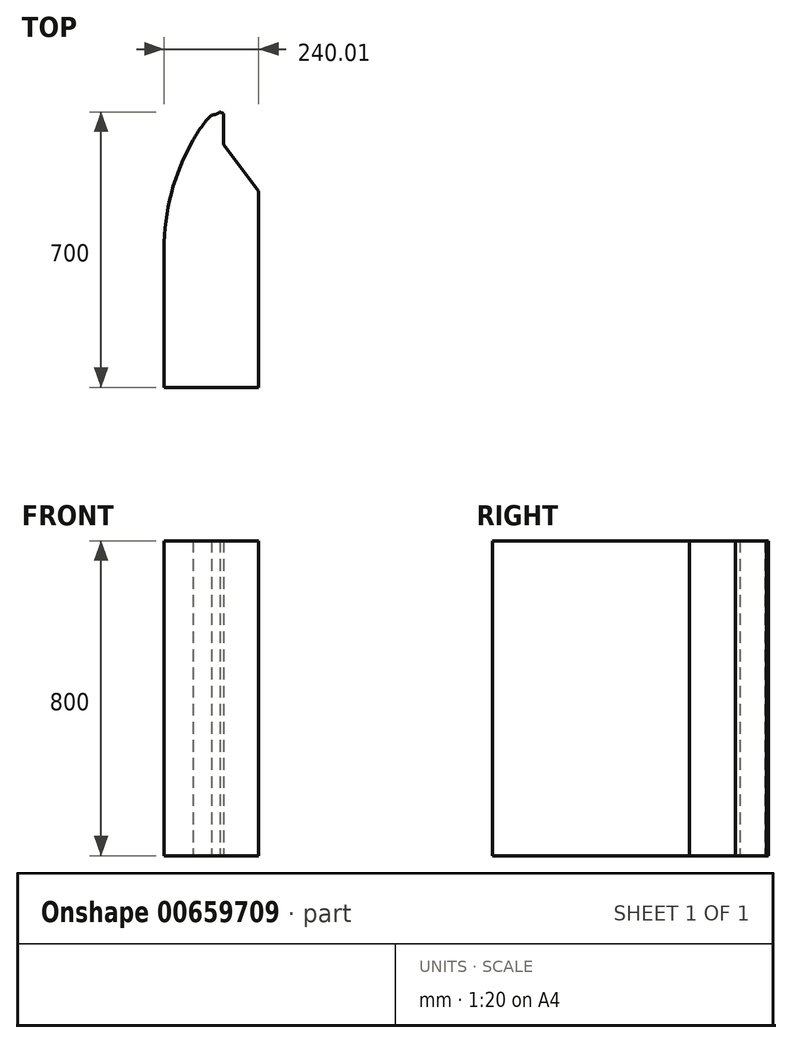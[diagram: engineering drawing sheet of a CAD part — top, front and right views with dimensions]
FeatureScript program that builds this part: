
annotation { "Feature Type Name" : "Feature", "Feature Type Description" : "" }
export const myFeature = defineFeature(function(context is Context, id is Id, definition is map)
    precondition{}
    {
        {
            var Q0;
            Q0=qCreatedBy(makeId("Top.planeOp"),FACE);
            var sketch = newSketch(context, id + "F0", { "sketchPlane" : qUnion([Q0])});
            skLineSegment(sketch, "E0.bottom", {"start": v(0, 0) * mm, "end": v(-240, 0) * mm});
            skLineSegment(sketch, "E0.left", {"start": v(0, 0) * mm, "end": v(0, 499.23) * mm});
            skLineSegment(sketch, "E0.right", {"start": v(-240, 0) * mm, "end": v(-240, 355.52) * mm});
            skLineSegment(sketch, "E1.bottom", {"start": v(0, 0) * mm, "end": v(-120, 0) * mm});
            skLineSegment(sketch, "E1.right", {"start": v(-120, 0) * mm, "end": v(-120, 691.92) * mm});
            skLineSegment(sketch, "E2", {"start": v(-89.05, 616.27) * mm, "end": v(0, 499.23) * mm});
            skPoint(sketch, "E3.orphan", {"position": v(0, 700) * mm});
            skLineSegment(sketch, "E4.top", {"start": v(-120, 0) * mm, "end": v(-98.03, 0) * mm});
            skLineSegment(sketch, "E4.left", {"start": v(-120, 691.92) * mm, "end": v(-120, 0) * mm});
            skLineSegment(sketch, "E4.right", {"start": v(-98.03, 700) * mm, "end": v(-98.03, 0) * mm});
            skArc(sketch, "E5", {"start": v(-120, 691.92) * mm, "mid": v(-108.3, 693.95) * mm, "end": v(-98.03, 699.94) * mm});
            skLineSegment(sketch, "E6", {"start": v(-98.03, 700) * mm, "end": v(-89.05, 695.23) * mm});
            skLineSegment(sketch, "E7", {"start": v(-89.05, 695.23) * mm, "end": v(-89.05, 0) * mm});
            skPoint(sketch, "E7.startSnap0", {"position": v(-89.05, 695.23) * mm});
            skPoint(sketch, "E8.orphan", {"position": v(-89.05, 703.2) * mm});
            skPoint(sketch, "E9.orphan", {"position": v(-80.07, 690.47) * mm});
            skArc(sketch, "E10", {"start": v(-166.34, 627.79) * mm, "mid": v(-221.63, 493.79) * mm, "end": v(-240, 350) * mm});
            skArc(sketch, "E11", {"start": v(-120, 691.92) * mm, "mid": v(-145.46, 661.5) * mm, "end": v(-166.34, 627.79) * mm});
            skPoint(sketch, "E0.top.start.orphan", {"position": v(-120, 700) * mm});
            skPoint(sketch, "E12.orphan", {"position": v(-240, 700) * mm});
            skSolve(sketch);
        }
        {
            var Q0;
            Q0 = qSketchRegion(id + "F0", true);
            extrude(context, id + "F1", {"entities" : qUnion([Q0]), "depth" : 800 * mm, "offsetDistance" : 25 * mm});
        }
    });
